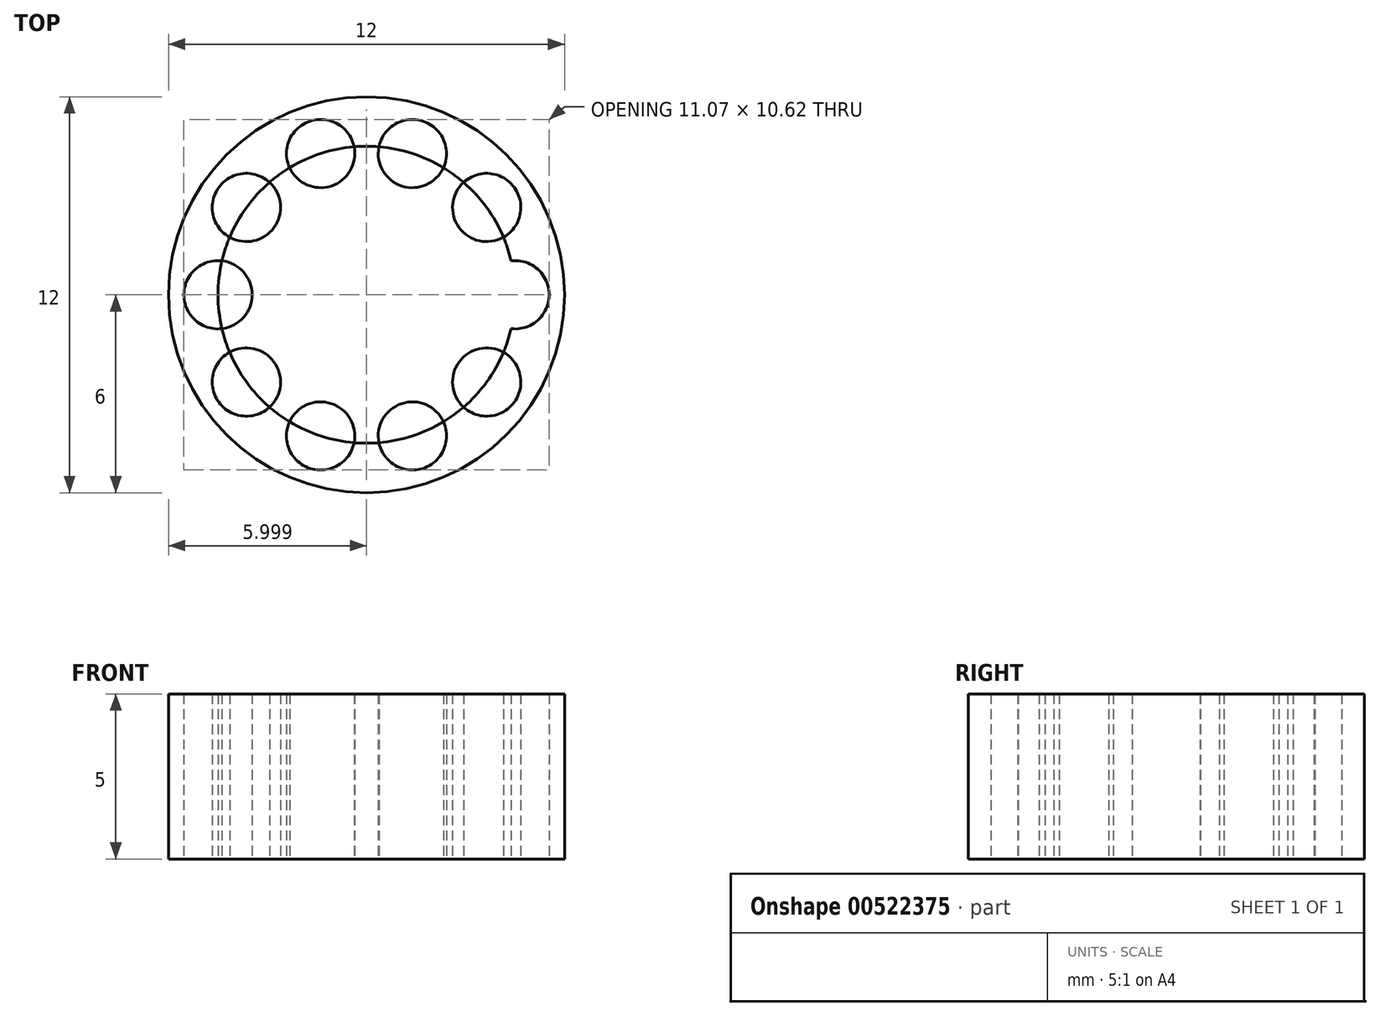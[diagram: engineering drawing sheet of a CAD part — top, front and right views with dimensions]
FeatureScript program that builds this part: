
annotation { "Feature Type Name" : "Feature", "Feature Type Description" : "" }
export const myFeature = defineFeature(function(context is Context, id is Id, definition is map)
    precondition{}
    {
        {
            var Q0;
            Q0=qCreatedBy(makeId("Top.planeOp"),FACE);
            var sketch = newSketch(context, id + "F0", { "sketchPlane" : qUnion([Q0])});
            skCircle(sketch, "E0", {"center": v(0.12, 0.08) * mm, "radius": 6 * mm});
            skCircle(sketch, "E1", {"center": v(0.12, 0.08) * mm, "radius": 4.5 * mm});
            skCircle(sketch, "E2", {"center": v(4.62, 0.08) * mm, "radius": 1.03 * mm});
            skCircle(sketch, "E3.1.0", {"center": v(3.76, 2.73) * mm, "radius": 1.03 * mm});
            skCircle(sketch, "E3.2.0", {"center": v(1.5, 4.36) * mm, "radius": 1.03 * mm});
            skCircle(sketch, "E3.3.0", {"center": v(-1.27, 4.36) * mm, "radius": 1.03 * mm});
            skCircle(sketch, "E3.4.0", {"center": v(-3.52, 2.73) * mm, "radius": 1.03 * mm});
            skCircle(sketch, "E3.5.0", {"center": v(-4.38, 0.08) * mm, "radius": 1.03 * mm});
            skCircle(sketch, "E3.6.0", {"center": v(-3.52, -2.56) * mm, "radius": 1.03 * mm});
            skCircle(sketch, "E3.7.0", {"center": v(-1.27, -4.2) * mm, "radius": 1.03 * mm});
            skCircle(sketch, "E3.8.0", {"center": v(1.5, -4.2) * mm, "radius": 1.03 * mm});
            skCircle(sketch, "E3.9.0", {"center": v(3.76, -2.56) * mm, "radius": 1.03 * mm});
            skSolve(sketch);
        }
        {
            var Q0;
            {var subQ0=sQuery(id+"F0.wireOp",EDGE,"E3.4.0");var subQ1=sQuery(id+"F0.wireOp",EDGE,"E1");var subQ2=makeQuery(id+"F0.imprint","INTERSECT",VERTEX,{"disambiguationData":[OD(0.0)],"derivedFrom":[subQ1,subQ0]});Q0=makeQuery(id+"F0.imprint","IMPRINT",FACE,{"disambiguationData":[TD([[makeQuery(id+"F0.imprint","IMPRINT",EDGE,{"disambiguationData":[TD([[subQ2,-1.0]])],"derivedFrom":subQ1}),1.0]])]});}
            var Q1;
            {var subQ0=sQuery(id+"F0.wireOp",EDGE,"E3.3.0");var subQ1=sQuery(id+"F0.wireOp",EDGE,"E1");var subQ2=makeQuery(id+"F0.imprint","INTERSECT",VERTEX,{"disambiguationData":[OD(0.0)],"derivedFrom":[subQ1,subQ0]});Q1=makeQuery(id+"F0.imprint","IMPRINT",FACE,{"disambiguationData":[TD([[makeQuery(id+"F0.imprint","IMPRINT",EDGE,{"disambiguationData":[TD([[subQ2,-1.0]])],"derivedFrom":subQ1}),1.0]])]});}
            var Q2;
            {var subQ0=sQuery(id+"F0.wireOp",EDGE,"E3.2.0");var subQ1=sQuery(id+"F0.wireOp",EDGE,"E1");var subQ2=makeQuery(id+"F0.imprint","INTERSECT",VERTEX,{"disambiguationData":[OD(0.0)],"derivedFrom":[subQ1,subQ0]});Q2=makeQuery(id+"F0.imprint","IMPRINT",FACE,{"disambiguationData":[TD([[makeQuery(id+"F0.imprint","IMPRINT",EDGE,{"disambiguationData":[TD([[subQ2,-1.0]])],"derivedFrom":subQ1}),1.0]])]});}
            var Q3;
            {var subQ0=sQuery(id+"F0.wireOp",EDGE,"E3.1.0");var subQ1=sQuery(id+"F0.wireOp",EDGE,"E1");var subQ2=makeQuery(id+"F0.imprint","INTERSECT",VERTEX,{"disambiguationData":[OD(0.0)],"derivedFrom":[subQ1,subQ0]});Q3=makeQuery(id+"F0.imprint","IMPRINT",FACE,{"disambiguationData":[TD([[makeQuery(id+"F0.imprint","IMPRINT",EDGE,{"disambiguationData":[TD([[subQ2,-1.0]])],"derivedFrom":subQ1}),1.0]])]});}
            var Q4;
            {var subQ0=sQuery(id+"F0.wireOp",EDGE,"E1");var subQ1=makeQuery(id+"F0.imprint","IMPRINT",VERTEX,{"derivedFrom":subQ0});Q4=makeQuery(id+"F0.imprint","IMPRINT",FACE,{"disambiguationData":[TD([[makeQuery(id+"F0.imprint","IMPRINT",EDGE,{"disambiguationData":[TD([[subQ1,-1.0]])],"derivedFrom":subQ0}),1.0]])]});}
            var Q5;
            {var subQ0=sQuery(id+"F0.wireOp",EDGE,"E3.9.0");var subQ1=sQuery(id+"F0.wireOp",EDGE,"E1");var subQ2=makeQuery(id+"F0.imprint","INTERSECT",VERTEX,{"disambiguationData":[OD(0.0)],"derivedFrom":[subQ1,subQ0]});Q5=makeQuery(id+"F0.imprint","IMPRINT",FACE,{"disambiguationData":[TD([[makeQuery(id+"F0.imprint","IMPRINT",EDGE,{"disambiguationData":[TD([[subQ2,-1.0]])],"derivedFrom":subQ1}),1.0]])]});}
            var Q6;
            {var subQ0=sQuery(id+"F0.wireOp",EDGE,"E3.8.0");var subQ1=sQuery(id+"F0.wireOp",EDGE,"E1");var subQ2=makeQuery(id+"F0.imprint","INTERSECT",VERTEX,{"disambiguationData":[OD(0.0)],"derivedFrom":[subQ1,subQ0]});Q6=makeQuery(id+"F0.imprint","IMPRINT",FACE,{"disambiguationData":[TD([[makeQuery(id+"F0.imprint","IMPRINT",EDGE,{"disambiguationData":[TD([[subQ2,-1.0]])],"derivedFrom":subQ1}),1.0]])]});}
            var Q7;
            {var subQ0=sQuery(id+"F0.wireOp",EDGE,"E3.7.0");var subQ1=sQuery(id+"F0.wireOp",EDGE,"E1");var subQ2=makeQuery(id+"F0.imprint","INTERSECT",VERTEX,{"disambiguationData":[OD(0.0)],"derivedFrom":[subQ1,subQ0]});Q7=makeQuery(id+"F0.imprint","IMPRINT",FACE,{"disambiguationData":[TD([[makeQuery(id+"F0.imprint","IMPRINT",EDGE,{"disambiguationData":[TD([[subQ2,-1.0]])],"derivedFrom":subQ1}),1.0]])]});}
            var Q8;
            {var subQ0=sQuery(id+"F0.wireOp",EDGE,"E3.6.0");var subQ1=sQuery(id+"F0.wireOp",EDGE,"E1");var subQ2=makeQuery(id+"F0.imprint","INTERSECT",VERTEX,{"disambiguationData":[OD(0.0)],"derivedFrom":[subQ1,subQ0]});Q8=makeQuery(id+"F0.imprint","IMPRINT",FACE,{"disambiguationData":[TD([[makeQuery(id+"F0.imprint","IMPRINT",EDGE,{"disambiguationData":[TD([[subQ2,-1.0]])],"derivedFrom":subQ1}),1.0]])]});}
            var Q9;
            {var subQ0=sQuery(id+"F0.wireOp",EDGE,"E3.5.0");var subQ1=sQuery(id+"F0.wireOp",EDGE,"E1");var subQ2=makeQuery(id+"F0.imprint","INTERSECT",VERTEX,{"disambiguationData":[OD(0.0)],"derivedFrom":[subQ1,subQ0]});Q9=makeQuery(id+"F0.imprint","IMPRINT",FACE,{"disambiguationData":[TD([[makeQuery(id+"F0.imprint","IMPRINT",EDGE,{"disambiguationData":[TD([[subQ2,-1.0]])],"derivedFrom":subQ1}),1.0]])]});}
            var Q10;
            Q10=makeQuery(id+"F0.imprint","IMPRINT",FACE,{"disambiguationData":[TD([[makeQuery(id+"F0.imprint","IMPRINT",EDGE,{"derivedFrom":sQuery(id+"F0.wireOp",EDGE,"E0")}),1.0]])]});
            var Q11;
            {var subQ0=sQuery(id+"F0.wireOp",EDGE,"E3.1.0");var subQ4=makeQuery(id+"F0.imprint","IMPRINT",VERTEX,{"derivedFrom":subQ0});Q11=makeQuery(id+"F0.imprint","IMPRINT",FACE,{"disambiguationData":[TD([[makeQuery(id+"F0.imprint","IMPRINT",EDGE,{"disambiguationData":[TD([[subQ4,-1.0]])],"derivedFrom":subQ0}),1.0]])]});}
            var Q12;
            {var subQ0=sQuery(id+"F0.wireOp",EDGE,"E3.2.0");var subQ4=makeQuery(id+"F0.imprint","IMPRINT",VERTEX,{"derivedFrom":subQ0});Q12=makeQuery(id+"F0.imprint","IMPRINT",FACE,{"disambiguationData":[TD([[makeQuery(id+"F0.imprint","IMPRINT",EDGE,{"disambiguationData":[TD([[subQ4,-1.0]])],"derivedFrom":subQ0}),1.0]])]});}
            var Q13;
            {var subQ0=sQuery(id+"F0.wireOp",EDGE,"E3.3.0");var subQ4=makeQuery(id+"F0.imprint","IMPRINT",VERTEX,{"derivedFrom":subQ0});Q13=makeQuery(id+"F0.imprint","IMPRINT",FACE,{"disambiguationData":[TD([[makeQuery(id+"F0.imprint","IMPRINT",EDGE,{"disambiguationData":[TD([[subQ4,1.0]])],"derivedFrom":subQ0}),1.0]])]});}
            var Q14;
            {var subQ0=sQuery(id+"F0.wireOp",EDGE,"E3.4.0");var subQ4=makeQuery(id+"F0.imprint","IMPRINT",VERTEX,{"derivedFrom":subQ0});Q14=makeQuery(id+"F0.imprint","IMPRINT",FACE,{"disambiguationData":[TD([[makeQuery(id+"F0.imprint","IMPRINT",EDGE,{"disambiguationData":[TD([[subQ4,1.0]])],"derivedFrom":subQ0}),1.0]])]});}
            var Q15;
            {var subQ0=sQuery(id+"F0.wireOp",EDGE,"E3.5.0");var subQ4=makeQuery(id+"F0.imprint","IMPRINT",VERTEX,{"derivedFrom":subQ0});Q15=makeQuery(id+"F0.imprint","IMPRINT",FACE,{"disambiguationData":[TD([[makeQuery(id+"F0.imprint","IMPRINT",EDGE,{"disambiguationData":[TD([[subQ4,1.0]])],"derivedFrom":subQ0}),1.0]])]});}
            var Q16;
            {var subQ0=sQuery(id+"F0.wireOp",EDGE,"E3.6.0");var subQ4=makeQuery(id+"F0.imprint","IMPRINT",VERTEX,{"derivedFrom":subQ0});Q16=makeQuery(id+"F0.imprint","IMPRINT",FACE,{"disambiguationData":[TD([[makeQuery(id+"F0.imprint","IMPRINT",EDGE,{"disambiguationData":[TD([[subQ4,1.0]])],"derivedFrom":subQ0}),1.0]])]});}
            var Q17;
            {var subQ0=sQuery(id+"F0.wireOp",EDGE,"E3.7.0");var subQ4=makeQuery(id+"F0.imprint","IMPRINT",VERTEX,{"derivedFrom":subQ0});Q17=makeQuery(id+"F0.imprint","IMPRINT",FACE,{"disambiguationData":[TD([[makeQuery(id+"F0.imprint","IMPRINT",EDGE,{"disambiguationData":[TD([[subQ4,1.0]])],"derivedFrom":subQ0}),1.0]])]});}
            var Q18;
            {var subQ0=sQuery(id+"F0.wireOp",EDGE,"E3.8.0");var subQ4=makeQuery(id+"F0.imprint","IMPRINT",VERTEX,{"derivedFrom":subQ0});Q18=makeQuery(id+"F0.imprint","IMPRINT",FACE,{"disambiguationData":[TD([[makeQuery(id+"F0.imprint","IMPRINT",EDGE,{"disambiguationData":[TD([[subQ4,1.0]])],"derivedFrom":subQ0}),1.0]])]});}
            var Q19;
            {var subQ0=sQuery(id+"F0.wireOp",EDGE,"E3.9.0");var subQ4=makeQuery(id+"F0.imprint","IMPRINT",VERTEX,{"derivedFrom":subQ0});Q19=makeQuery(id+"F0.imprint","IMPRINT",FACE,{"disambiguationData":[TD([[makeQuery(id+"F0.imprint","IMPRINT",EDGE,{"disambiguationData":[TD([[subQ4,1.0]])],"derivedFrom":subQ0}),1.0]])]});}
            var Q20;
            {var subQ0=sQuery(id+"F0.wireOp",EDGE,"E1");var subQ1=makeQuery(id+"F0.imprint","IMPRINT",VERTEX,{"derivedFrom":subQ0});Q20=makeQuery(id+"F0.imprint","IMPRINT",FACE,{"disambiguationData":[TD([[makeQuery(id+"F0.imprint","IMPRINT",EDGE,{"disambiguationData":[TD([[subQ1,-1.0]])],"derivedFrom":subQ0}),-1.0]])]});}
            extrude(context, id + "F1", {"entities" : qUnion([Q0, Q1, Q2, Q3, Q4, Q5, Q6, Q7, Q8, Q9, Q10, Q11, Q12, Q13, Q14, Q15, Q16, Q17, Q18, Q19, Q20]), "depth" : 5 * mm, "offsetDistance" : 25 * mm});
        }
    });
